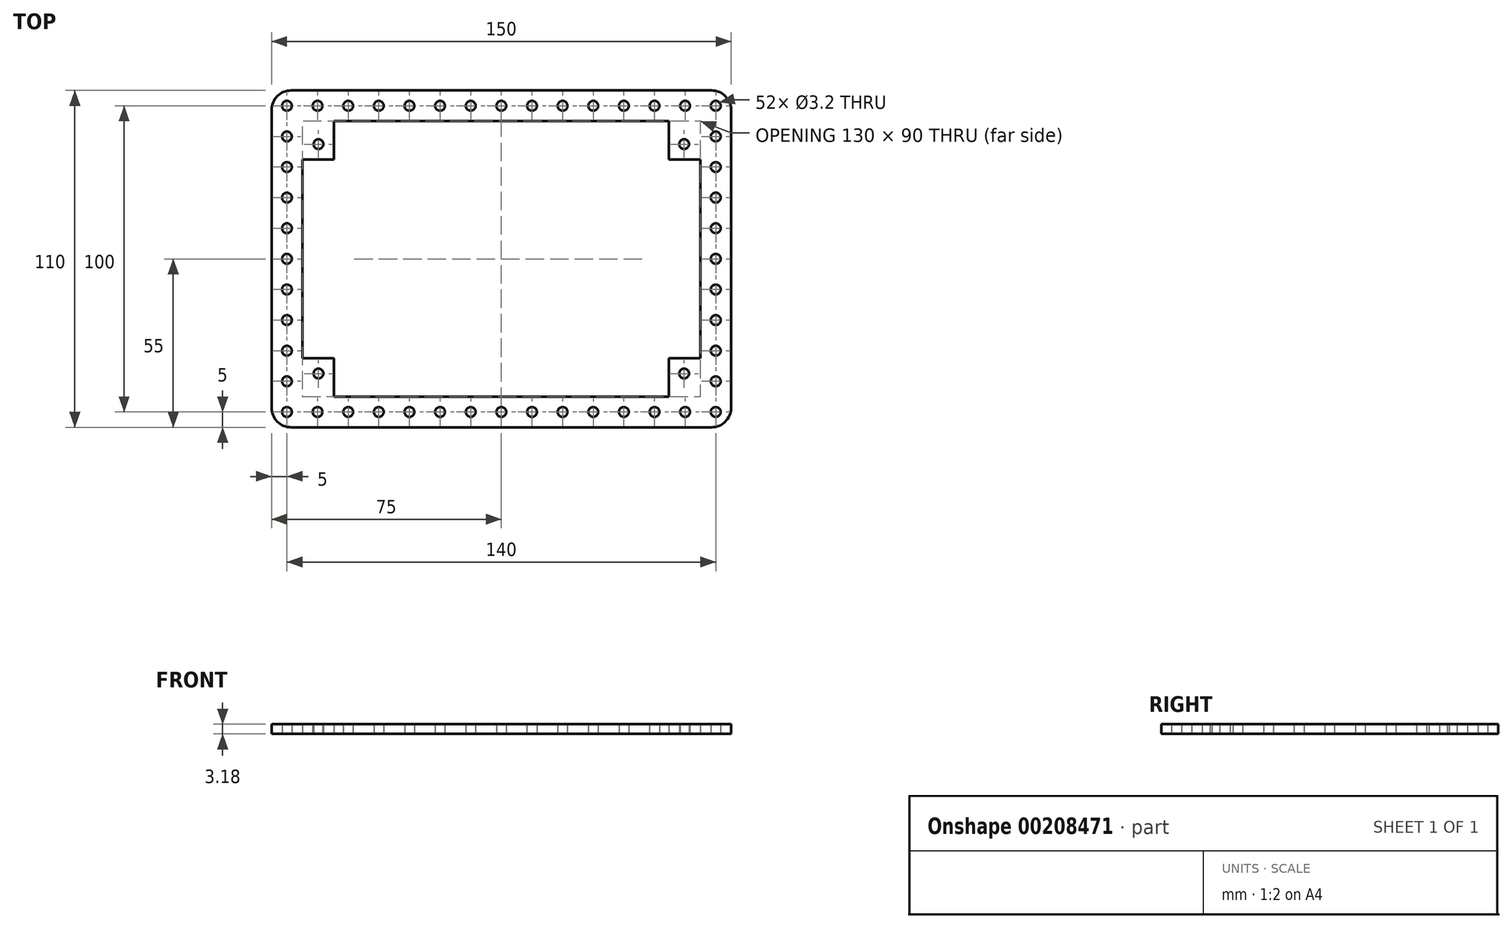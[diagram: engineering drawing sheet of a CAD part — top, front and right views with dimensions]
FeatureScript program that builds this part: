
annotation { "Feature Type Name" : "Feature", "Feature Type Description" : "" }
export const myFeature = defineFeature(function(context is Context, id is Id, definition is map)
    precondition{}
    {
        {
            var Q0;
            Q0=qCreatedBy(makeId("Top.planeOp"),FACE);
            var sketch = newSketch(context, id + "F0", { "sketchPlane" : qUnion([Q0])});
            skLineSegment(sketch, "E0.bottom", {"start": v(6.35, 0) * mm, "end": v(143.65, 0) * mm});
            skLineSegment(sketch, "E0.top", {"start": v(6.35, 110) * mm, "end": v(143.65, 110) * mm});
            skLineSegment(sketch, "E0.left", {"start": v(0, 6.35) * mm, "end": v(0, 103.65) * mm});
            skLineSegment(sketch, "E0.right", {"start": v(150, 6.35) * mm, "end": v(150, 103.65) * mm});
            skPoint(sketch, "E1.visualSharp", {"position": v(0, 110) * mm});
            skArc(sketch, "E1.filletArc", {"start": v(6.35, 110) * mm, "mid": v(1.86, 108.14) * mm, "end": v(0, 103.65) * mm});
            skPoint(sketch, "E2.visualSharp", {"position": v(150, 110) * mm});
            skArc(sketch, "E2.filletArc", {"start": v(150, 103.65) * mm, "mid": v(148.14, 108.14) * mm, "end": v(143.65, 110) * mm});
            skPoint(sketch, "E3.visualSharp", {"position": v(150, 0) * mm});
            skArc(sketch, "E3.filletArc", {"start": v(143.65, 0) * mm, "mid": v(148.14, 1.86) * mm, "end": v(150, 6.35) * mm});
            skPoint(sketch, "E4.visualSharp", {"position": v(0, 0) * mm});
            skArc(sketch, "E4.filletArc", {"start": v(0, 6.35) * mm, "mid": v(1.86, 1.86) * mm, "end": v(6.35, 0) * mm});
            skCircle(sketch, "E5", {"center": v(15.31, 17.54) * mm, "radius": 1.6 * mm});
            skCircle(sketch, "E6", {"center": v(15.31, 92.47) * mm, "radius": 1.6 * mm});
            skCircle(sketch, "E7", {"center": v(134.7, 92.47) * mm, "radius": 1.6 * mm});
            skCircle(sketch, "E8", {"center": v(134.7, 17.54) * mm, "radius": 1.6 * mm});
            skLineSegment(sketch, "E9.bottom", {"start": v(10, 22.54) * mm, "end": v(20.31, 22.54) * mm});
            skLineSegment(sketch, "E9.top", {"start": v(10, 87.47) * mm, "end": v(20.31, 87.47) * mm});
            skLineSegment(sketch, "E9.left", {"start": v(10, 22.54) * mm, "end": v(10, 87.46) * mm});
            skLineSegment(sketch, "E9.right", {"start": v(140, 22.54) * mm, "end": v(140, 87.47) * mm});
            skLineSegment(sketch, "E10.top", {"start": v(20.31, 100) * mm, "end": v(129.7, 100) * mm});
            skLineSegment(sketch, "E10.left", {"start": v(20.31, 87.47) * mm, "end": v(20.31, 100) * mm});
            skLineSegment(sketch, "E10.right", {"start": v(129.7, 87.47) * mm, "end": v(129.7, 100) * mm});
            skLineSegment(sketch, "E11.top", {"start": v(20.31, 10) * mm, "end": v(129.7, 10) * mm});
            skLineSegment(sketch, "E11.left", {"start": v(20.31, 22.54) * mm, "end": v(20.31, 10) * mm});
            skLineSegment(sketch, "E11.right", {"start": v(129.7, 22.54) * mm, "end": v(129.7, 10) * mm});
            skLineSegment(sketch, "E12.trimOffspring", {"start": v(129.7, 22.54) * mm, "end": v(140, 22.54) * mm});
            skLineSegment(sketch, "E13.trimOffspring", {"start": v(129.7, 87.47) * mm, "end": v(140, 87.47) * mm});
            skCircle(sketch, "E14", {"center": v(5, 105) * mm, "radius": 1.6 * mm});
            skCircle(sketch, "E15.1.0.0", {"center": v(15, 105) * mm, "radius": 1.6 * mm});
            skCircle(sketch, "E15.2.0.0", {"center": v(25, 105) * mm, "radius": 1.6 * mm});
            skCircle(sketch, "E15.3.0.0", {"center": v(35, 105) * mm, "radius": 1.6 * mm});
            skCircle(sketch, "E15.4.0.0", {"center": v(45, 105) * mm, "radius": 1.6 * mm});
            skCircle(sketch, "E15.5.0.0", {"center": v(55, 105) * mm, "radius": 1.6 * mm});
            skCircle(sketch, "E15.6.0.0", {"center": v(65, 105) * mm, "radius": 1.6 * mm});
            skCircle(sketch, "E15.7.0.0", {"center": v(75, 105) * mm, "radius": 1.6 * mm});
            skCircle(sketch, "E15.8.0.0", {"center": v(85, 105) * mm, "radius": 1.6 * mm});
            skCircle(sketch, "E15.9.0.0", {"center": v(95, 105) * mm, "radius": 1.6 * mm});
            skCircle(sketch, "E15.10.0.0", {"center": v(105, 105) * mm, "radius": 1.6 * mm});
            skCircle(sketch, "E15.11.0.0", {"center": v(115, 105) * mm, "radius": 1.6 * mm});
            skCircle(sketch, "E15.12.0.0", {"center": v(125, 105) * mm, "radius": 1.6 * mm});
            skCircle(sketch, "E15.13.0.0", {"center": v(135, 105) * mm, "radius": 1.6 * mm});
            skCircle(sketch, "E15.14.0.0", {"center": v(145, 105) * mm, "radius": 1.6 * mm});
            skLineSegment(sketch, "E15.direction1", {"start": v(5, 105) * mm, "end": v(15, 105) * mm, "construction": true});
            skCircle(sketch, "E16.0.1.0", {"center": v(5, 95) * mm, "radius": 1.6 * mm});
            skCircle(sketch, "E16.0.2.0", {"center": v(5, 85) * mm, "radius": 1.6 * mm});
            skCircle(sketch, "E16.0.3.0", {"center": v(5, 75) * mm, "radius": 1.6 * mm});
            skCircle(sketch, "E16.0.4.0", {"center": v(5, 65) * mm, "radius": 1.6 * mm});
            skCircle(sketch, "E16.0.5.0", {"center": v(5, 55) * mm, "radius": 1.6 * mm});
            skCircle(sketch, "E16.0.6.0", {"center": v(5, 45) * mm, "radius": 1.6 * mm});
            skCircle(sketch, "E16.0.7.0", {"center": v(5, 35) * mm, "radius": 1.6 * mm});
            skCircle(sketch, "E16.0.8.0", {"center": v(5, 25) * mm, "radius": 1.6 * mm});
            skCircle(sketch, "E16.0.9.0", {"center": v(5, 15) * mm, "radius": 1.6 * mm});
            skCircle(sketch, "E16.0.10.0", {"center": v(5, 5) * mm, "radius": 1.6 * mm});
            skLineSegment(sketch, "E16.direction1", {"start": v(5, 105) * mm, "end": v(30, 105) * mm, "construction": true});
            skLineSegment(sketch, "E16.direction2", {"start": v(5, 105) * mm, "end": v(5, 95) * mm, "construction": true});
            skCircle(sketch, "E17", {"center": v(145, 5) * mm, "radius": 1.6 * mm});
            skCircle(sketch, "E18.1.0.0", {"center": v(135, 5) * mm, "radius": 1.6 * mm});
            skCircle(sketch, "E18.2.0.0", {"center": v(125, 5) * mm, "radius": 1.6 * mm});
            skCircle(sketch, "E18.3.0.0", {"center": v(115, 5) * mm, "radius": 1.6 * mm});
            skCircle(sketch, "E18.4.0.0", {"center": v(105, 5) * mm, "radius": 1.6 * mm});
            skCircle(sketch, "E18.5.0.0", {"center": v(95, 5) * mm, "radius": 1.6 * mm});
            skCircle(sketch, "E18.6.0.0", {"center": v(85, 5) * mm, "radius": 1.6 * mm});
            skCircle(sketch, "E18.7.0.0", {"center": v(75, 5) * mm, "radius": 1.6 * mm});
            skCircle(sketch, "E18.8.0.0", {"center": v(65, 5) * mm, "radius": 1.6 * mm});
            skCircle(sketch, "E18.9.0.0", {"center": v(55, 5) * mm, "radius": 1.6 * mm});
            skCircle(sketch, "E18.10.0.0", {"center": v(45, 5) * mm, "radius": 1.6 * mm});
            skCircle(sketch, "E18.11.0.0", {"center": v(35, 5) * mm, "radius": 1.6 * mm});
            skCircle(sketch, "E18.12.0.0", {"center": v(25, 5) * mm, "radius": 1.6 * mm});
            skCircle(sketch, "E18.13.0.0", {"center": v(15, 5) * mm, "radius": 1.6 * mm});
            skLineSegment(sketch, "E18.direction1", {"start": v(145, 5) * mm, "end": v(135, 5) * mm, "construction": true});
            skCircle(sketch, "E19.0.1.0", {"center": v(145, 15) * mm, "radius": 1.6 * mm});
            skCircle(sketch, "E19.0.2.0", {"center": v(145, 25) * mm, "radius": 1.6 * mm});
            skCircle(sketch, "E19.0.3.0", {"center": v(145, 35) * mm, "radius": 1.6 * mm});
            skCircle(sketch, "E19.0.4.0", {"center": v(145, 45) * mm, "radius": 1.6 * mm});
            skCircle(sketch, "E19.0.5.0", {"center": v(145, 55) * mm, "radius": 1.6 * mm});
            skCircle(sketch, "E19.0.6.0", {"center": v(145, 65) * mm, "radius": 1.6 * mm});
            skCircle(sketch, "E19.0.7.0", {"center": v(145, 75) * mm, "radius": 1.6 * mm});
            skCircle(sketch, "E19.0.8.0", {"center": v(145, 85) * mm, "radius": 1.6 * mm});
            skCircle(sketch, "E19.0.9.0", {"center": v(145, 95) * mm, "radius": 1.6 * mm});
            skLineSegment(sketch, "E19.direction1", {"start": v(145, 5) * mm, "end": v(170, 5) * mm, "construction": true});
            skLineSegment(sketch, "E19.direction2", {"start": v(145, 5) * mm, "end": v(145, 15) * mm, "construction": true});
            skSolve(sketch);
        }
        {
            var Q0;
            Q0=qSketchRegion(id+"F0",true);
            extrude(context, id + "F1", {"entities" : qUnion([Q0]), "depth" : 3.17 * mm});
        }
    });
